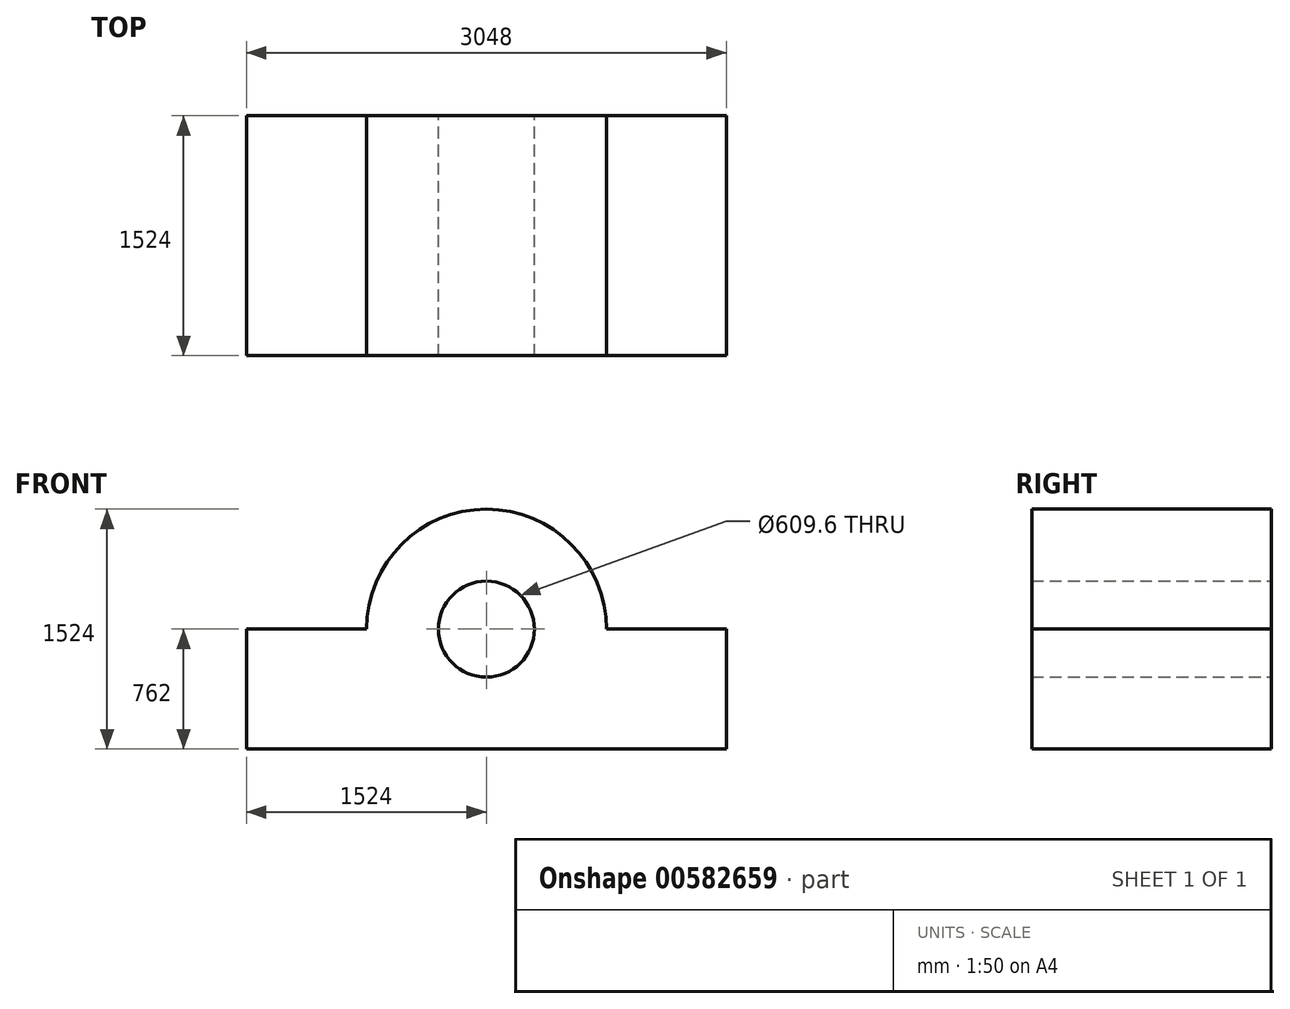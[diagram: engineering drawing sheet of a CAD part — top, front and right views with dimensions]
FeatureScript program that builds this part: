
annotation { "Feature Type Name" : "Feature", "Feature Type Description" : "" }
export const myFeature = defineFeature(function(context is Context, id is Id, definition is map)
    precondition{}
    {
        {
            var Q0;
            Q0=qCreatedBy(makeId("Front.planeOp"),FACE);
            var sketch = newSketch(context, id + "F0", { "sketchPlane" : qUnion([Q0])});
            skLineSegment(sketch, "E0", {"start": v(0, 0) * mm, "end": v(3048, 0) * mm});
            skLineSegment(sketch, "E1", {"start": v(3048, 0) * mm, "end": v(3048, 762) * mm});
            skLineSegment(sketch, "E2", {"start": v(3048, 762) * mm, "end": v(2286, 762) * mm});
            skLineSegment(sketch, "E3", {"start": v(0, 762) * mm, "end": v(0, 0) * mm});
            skArc(sketch, "E4", {"start": v(2286, 762) * mm, "mid": v(1524, 1524) * mm, "end": v(762, 762) * mm});
            skCircle(sketch, "E5", {"center": v(1524, 762) * mm, "radius": 304.8 * mm});
            skLineSegment(sketch, "E6.trimOffspring", {"start": v(762, 762) * mm, "end": v(0, 762) * mm});
            skSolve(sketch);
        }
        {
            var Q0;
            Q0=makeQuery(id+"F0.imprint","IMPRINT",FACE,{"disambiguationData":[TD([[makeQuery(id+"F0.imprint","IMPRINT",EDGE,{"derivedFrom":sQuery(id+"F0.wireOp",EDGE,"E0")}),1.0]])]});
            extrude(context, id + "F1", {"entities" : qUnion([Q0]), "depth" : 1524 * mm, "offsetDistance" : 25.4 * mm});
        }
    });
